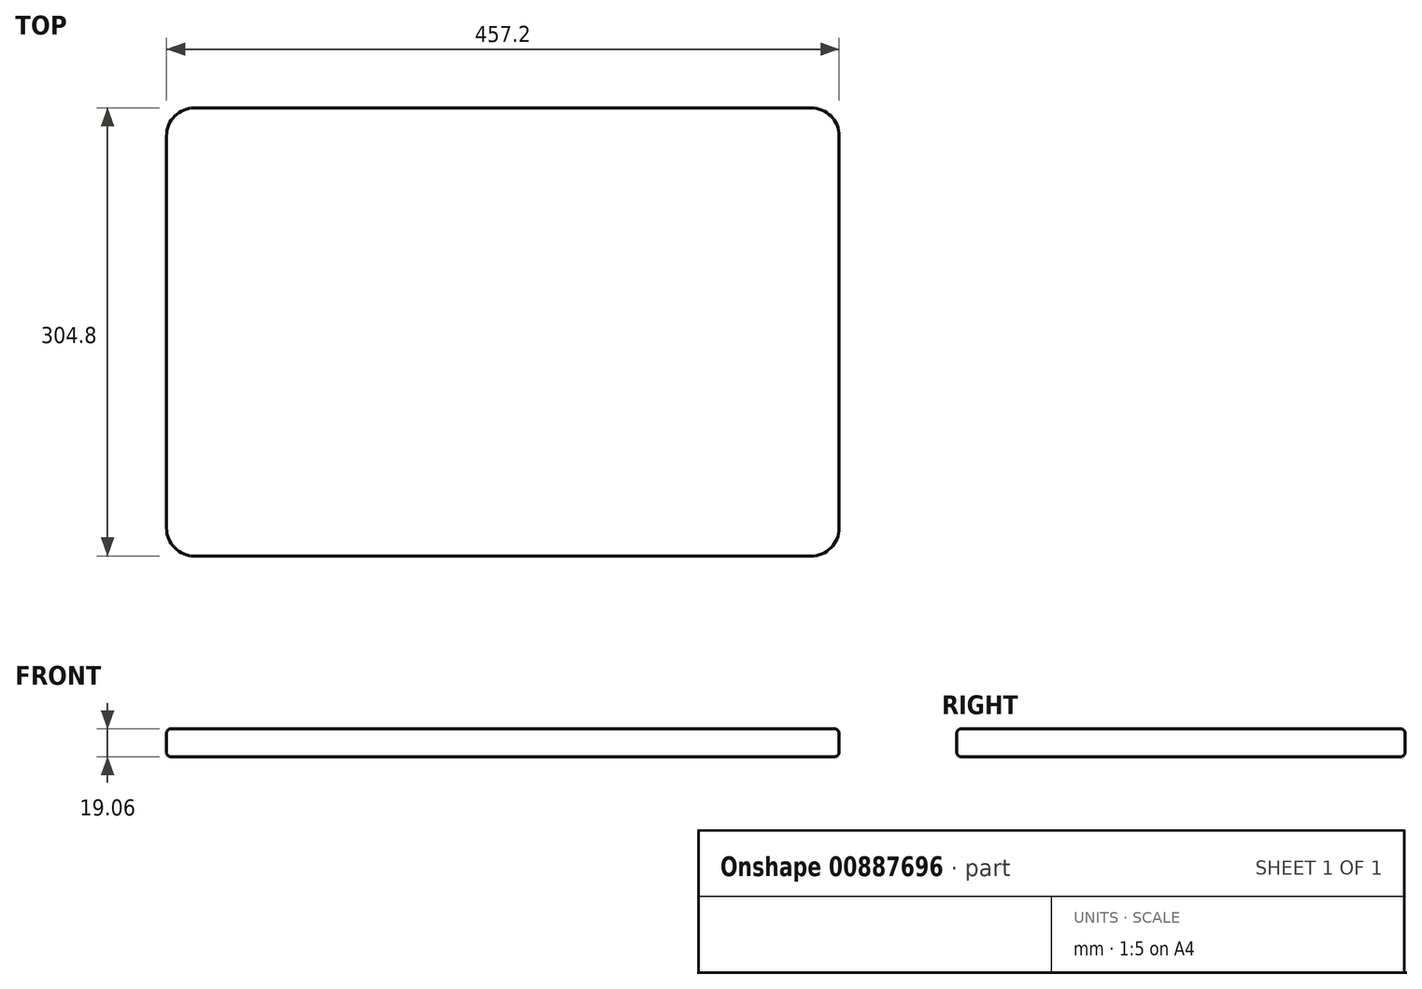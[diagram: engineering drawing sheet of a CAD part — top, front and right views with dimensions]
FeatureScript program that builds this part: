
annotation { "Feature Type Name" : "Feature", "Feature Type Description" : "" }
export const myFeature = defineFeature(function(context is Context, id is Id, definition is map)
    precondition{}
    {
        {
            var Q0;
            Q0=qCreatedBy(makeId("Top.planeOp"),FACE);
            var sketch = newSketch(context, id + "F0", { "sketchPlane" : qUnion([Q0])});
            skLineSegment(sketch, "E0.bottom", {"start": v(228.6, 152.4) * mm, "end": v(-228.6, 152.4) * mm});
            skLineSegment(sketch, "E0.top", {"start": v(228.6, -152.4) * mm, "end": v(-228.6, -152.4) * mm});
            skLineSegment(sketch, "E0.left", {"start": v(228.6, 152.4) * mm, "end": v(228.6, -152.4) * mm});
            skLineSegment(sketch, "E0.right", {"start": v(-228.6, 152.4) * mm, "end": v(-228.6, -152.4) * mm});
            skPoint(sketch, "E0.middle", {"position": v(0, 0) * mm});
            skSolve(sketch);
        }
        {
            var Q0;
            Q0=makeQuery(id+"F0.imprint","IMPRINT",FACE,{"disambiguationData":[TD([[makeQuery(id+"F0.imprint","IMPRINT",EDGE,{"derivedFrom":sQuery(id+"F0.wireOp",EDGE,"E0.bottom")}),1.0]])]});
            extrude(context, id + "F1", {"entities" : qUnion([Q0]), "endBound" : BoundingType.SYMMETRIC, "depth" : 19.05 * mm, "offsetDistance" : 25.4 * mm});
        }
        {
            var Q0;
            Q0=makeQuery(id+"F1.opExtrude","SWEPT_EDGE",EDGE,{"disambiguationData":[OSD([sQuery(id+"F0.wireOp",EDGE,"E0.top"),sQuery(id+"F0.wireOp",EDGE,"E0.right")])]});
            var Q1;
            Q1=makeQuery(id+"F1.opExtrude","SWEPT_EDGE",EDGE,{"disambiguationData":[OSD([sQuery(id+"F0.wireOp",EDGE,"E0.top"),sQuery(id+"F0.wireOp",EDGE,"E0.left")])]});
            var Q2;
            Q2=makeQuery(id+"F1.opExtrude","SWEPT_EDGE",EDGE,{"disambiguationData":[OSD([sQuery(id+"F0.wireOp",EDGE,"E0.bottom"),sQuery(id+"F0.wireOp",EDGE,"E0.left")])]});
            var Q3;
            Q3=makeQuery(id+"F1.opExtrude","SWEPT_EDGE",EDGE,{"disambiguationData":[OSD([sQuery(id+"F0.wireOp",EDGE,"E0.bottom"),sQuery(id+"F0.wireOp",EDGE,"E0.right")])]});
            fillet(context, id + "F2", {"entities" : qUnion([Q0, Q1, Q2, Q3]), "radius" : 19.05 * mm, "tangentPropagation" : true, "allowEdgeOverflow" : false});
        }
        {
            var Q0;
            Q0=makeQuery(id+"F1.opExtrude","CAP_FACE",FACE,{"disambiguationData":[OSD([sQuery(id+"F0.wireOp",EDGE,"E0.bottom"),sQuery(id+"F0.wireOp",EDGE,"E0.top"),sQuery(id+"F0.wireOp",EDGE,"E0.left"),sQuery(id+"F0.wireOp",EDGE,"E0.right")])],"isStart":false});
            var Q1;
            Q1=makeQuery(id+"F1.opExtrude","CAP_FACE",FACE,{"disambiguationData":[OSD([sQuery(id+"F0.wireOp",EDGE,"E0.bottom"),sQuery(id+"F0.wireOp",EDGE,"E0.top"),sQuery(id+"F0.wireOp",EDGE,"E0.left"),sQuery(id+"F0.wireOp",EDGE,"E0.right")])],"isStart":true});
            fillet(context, id + "F3", {"entities" : qUnion([Q0, Q1]), "radius" : 3.17 * mm, "tangentPropagation" : true, "allowEdgeOverflow" : false});
        }
    });
